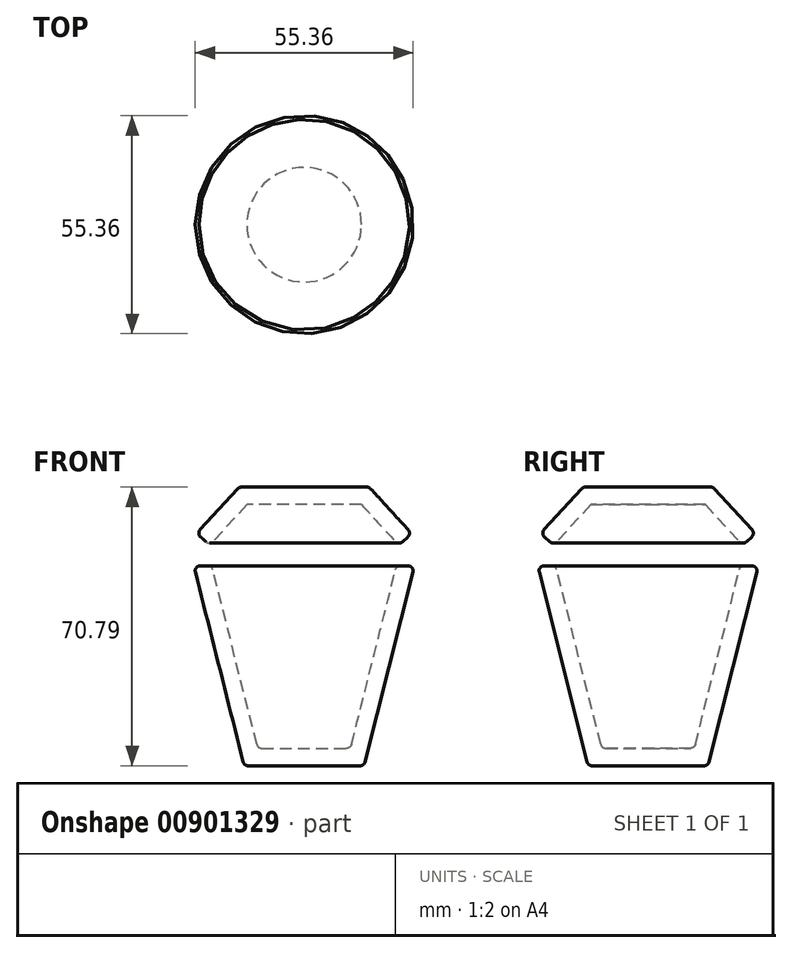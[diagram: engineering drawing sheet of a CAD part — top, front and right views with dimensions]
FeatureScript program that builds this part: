
annotation { "Feature Type Name" : "Feature", "Feature Type Description" : "" }
export const myFeature = defineFeature(function(context is Context, id is Id, definition is map)
    precondition{}
    {
        {
            var Q0;
            Q0=qCreatedBy(makeId("Right.planeOp"),FACE);
            var sketch = newSketch(context, id + "F0", { "sketchPlane" : qUnion([Q0])});
            skLineSegment(sketch, "E0", {"start": v(0, 0) * mm, "end": v(-15.24, 0) * mm});
            skLineSegment(sketch, "E1", {"start": v(-15.24, 0) * mm, "end": v(-28.04, 50.8) * mm});
            skLineSegment(sketch, "E2", {"start": v(-28.04, 50.8) * mm, "end": v(-23.46, 50.8) * mm});
            skLineSegment(sketch, "E3", {"start": v(-23.46, 50.8) * mm, "end": v(-11.78, 4.44) * mm});
            skLineSegment(sketch, "E4", {"start": v(-11.78, 4.44) * mm, "end": v(0, 4.44) * mm});
            skLineSegment(sketch, "E5", {"start": v(0, 4.44) * mm, "end": v(0, 0) * mm});
            skLineSegment(sketch, "E6", {"start": v(-24, 56.04) * mm, "end": v(-14.55, 66.35) * mm});
            skLineSegment(sketch, "E7", {"start": v(-14.55, 66.35) * mm, "end": v(0, 66.35) * mm});
            skLineSegment(sketch, "E8", {"start": v(0, 66.35) * mm, "end": v(0, 70.8) * mm});
            skLineSegment(sketch, "E9", {"start": v(0, 70.8) * mm, "end": v(-16.51, 70.8) * mm});
            skLineSegment(sketch, "E10", {"start": v(-16.51, 70.8) * mm, "end": v(-27.28, 59.05) * mm});
            skLineSegment(sketch, "E11", {"start": v(-27.28, 59.05) * mm, "end": v(-24, 56.04) * mm});
            skSolve(sketch);
        }
        {
            var Q0;
            Q0 = qSketchRegion(id + "F0", true);
            var Q1;
            Q1=sQuery(id+"F0.wireOp",EDGE,"E5");
            revolve(context, id + "F1", {"surfaceOperationType" : NewSurfaceOperationType.NEW, "entities" : qUnion([Q0]), "axis" : qUnion([Q1]), "revolveType" : RevolveType.FULL});
        }
        {
            var Q0;
            Q0=makeQuery(id+"F1.opRevolve","SWEPT_EDGE",EDGE,{"disambiguationData":[OSD([sQuery(id+"F0.wireOp",EDGE,"E1"),sQuery(id+"F0.wireOp",EDGE,"E2")])]});
            var Q1;
            Q1=makeQuery(id+"F1.opRevolve","SWEPT_EDGE",EDGE,{"disambiguationData":[OSD([sQuery(id+"F0.wireOp",EDGE,"E2"),sQuery(id+"F0.wireOp",EDGE,"E3")])]});
            var Q2;
            Q2=makeQuery(id+"F1.opRevolve","SWEPT_FACE",FACE,{"disambiguationData":[OSD([sQuery(id+"F0.wireOp",EDGE,"E4")])]});
            var Q3;
            Q3=makeQuery(id+"F1.opRevolve","SWEPT_EDGE",EDGE,{"disambiguationData":[OSD([sQuery(id+"F0.wireOp",EDGE,"E0"),sQuery(id+"F0.wireOp",EDGE,"E1")])]});
            var Q4;
            Q4=makeQuery(id+"F1.opRevolve","SWEPT_EDGE",EDGE,{"disambiguationData":[OSD([sQuery(id+"F0.wireOp",EDGE,"E10"),sQuery(id+"F0.wireOp",EDGE,"E11")])]});
            var Q5;
            Q5=makeQuery(id+"F1.opRevolve","SWEPT_EDGE",EDGE,{"disambiguationData":[OSD([sQuery(id+"F0.wireOp",EDGE,"E6"),sQuery(id+"F0.wireOp",EDGE,"E11")])]});
            var Q6;
            Q6=makeQuery(id+"F1.opRevolve","SWEPT_EDGE",EDGE,{"disambiguationData":[OSD([sQuery(id+"F0.wireOp",EDGE,"E9"),sQuery(id+"F0.wireOp",EDGE,"E10")])]});
            fillet(context, id + "F2", {"entities" : qUnion([Q0, Q1, Q2, Q3, Q4, Q5, Q6]), "radius" : 1.27 * mm, "tangentPropagation" : true, "allowEdgeOverflow" : false});
        }
    });
